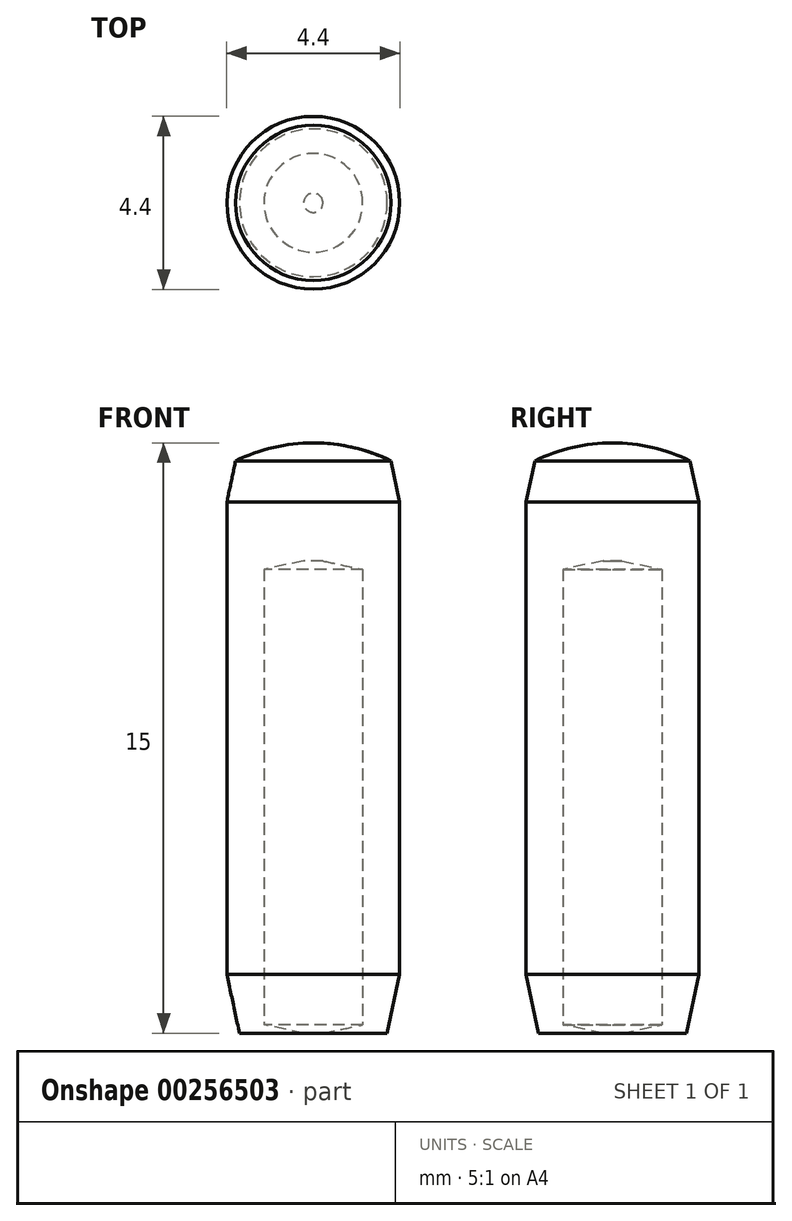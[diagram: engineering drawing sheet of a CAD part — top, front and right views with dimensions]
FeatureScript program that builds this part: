
annotation { "Feature Type Name" : "Feature", "Feature Type Description" : "" }
export const myFeature = defineFeature(function(context is Context, id is Id, definition is map)
    precondition{}
    {
        {
            var Q0;
            Q0=qCreatedBy(makeId("Top.planeOp"),FACE);
            var sketch = newSketch(context, id + "F0", { "sketchPlane" : qUnion([Q0])});
            skCircle(sketch, "E0", {"center": v(0, 0) * mm, "radius": 0.42 * mm});
            skSolve(sketch);
        }
        {
            var Q0;
            Q0=qSketchRegion(id+"F0",true);
            extrude(context, id + "F1", {"entities" : qUnion([Q0]), "depth" : 4 * mm});
        }
        {
            var Q0;
            Q0=makeQuery(id+"F1.opExtrude","CAP_EDGE",EDGE,{"disambiguationData":[OSD([sQuery(id+"F0.wireOp",EDGE,"E0")])],"isStart":false});
            var Q1;
            Q1=makeQuery(id+"F1.opExtrude","CAP_EDGE",EDGE,{"disambiguationData":[OSD([sQuery(id+"F0.wireOp",EDGE,"E0")])],"isStart":true});
            chamfer(context, id + "F2", {"entities" : qUnion([Q0, Q1]), "chamferType" : ChamferType.OFFSET_ANGLE, "width" : 0.5 * mm, "oppositeDirection" : true, "angle" : 12 * degree, "tangentPropagation" : true});
        }
        {
            var Q0;
            Q0=qCreatedBy(makeId("Front.planeOp"),FACE);
            var sketch = newSketch(context, id + "F3", { "sketchPlane" : qUnion([Q0])});
            skLineSegment(sketch, "E1", {"start": v(0, 0) * mm, "end": v(0, 5) * mm});
            skLineSegment(sketch, "E2", {"start": v(0.73, 4.5) * mm, "end": v(0.73, 0.5) * mm});
            skArc(sketch, "E3", {"start": v(0.66, 4.85) * mm, "mid": v(0.34, 4.96) * mm, "end": v(0, 5) * mm});
            skLineSegment(sketch, "E4", {"start": v(0.73, 4.5) * mm, "end": v(0.66, 4.85) * mm});
            skPoint(sketch, "E5", {"position": v(0, 2.5) * mm});
            skLineSegment(sketch, "E6", {"start": v(0.73, 0.5) * mm, "end": v(0.63, 0) * mm});
            skLineSegment(sketch, "E7", {"start": v(0, 0) * mm, "end": v(0.63, 0) * mm});
            skSolve(sketch);
        }
        {
            var Q0;
            Q0=makeQuery(id+"F3.imprint","IMPRINT",FACE,{"disambiguationData":[TD([[makeQuery(id+"F3.imprint","IMPRINT",EDGE,{"derivedFrom":sQuery(id+"F3.wireOp",EDGE,"E1")}),-1.0]])]});
            var Q1;
            Q1=sQuery(id+"F3.wireOp",EDGE,"E1");
            revolve(context, id + "F4", {"entities" : qUnion([Q0]), "axis" : qUnion([Q1]), "revolveType" : RevolveType.FULL});
        }
        {
            var Q0;
            Q0=makeQuery(id+"F1.opExtrude","SWEPT_BODY",BODY,{"disambiguationData":[OSD([sQuery(id+"F0.wireOp",EDGE,"E0")])]});
            var Q1;
            Q1=makeQuery(id+"F4.opRevolve","SWEPT_BODY",BODY,{"disambiguationData":[OSD([sQuery(id+"F3.wireOp",EDGE,"E1"),sQuery(id+"F3.wireOp",EDGE,"E2"),sQuery(id+"F3.wireOp",EDGE,"E3"),sQuery(id+"F3.wireOp",EDGE,"E4"),sQuery(id+"F3.wireOp",EDGE,"E6"),sQuery(id+"F3.wireOp",EDGE,"E7")])]});
            var Q2;
            Q2=qCreatedBy(makeId("Origin.pointOp"),VERTEX);
            transform(context, id + "F5", {"entities" : qUnion([Q0, Q1]), "transformType" : TransformType.SCALE_UNIFORMLY, "scale" : 3, "makeCopy" : false, "scalePoint" : qUnion([Q2])});
        }
    });
